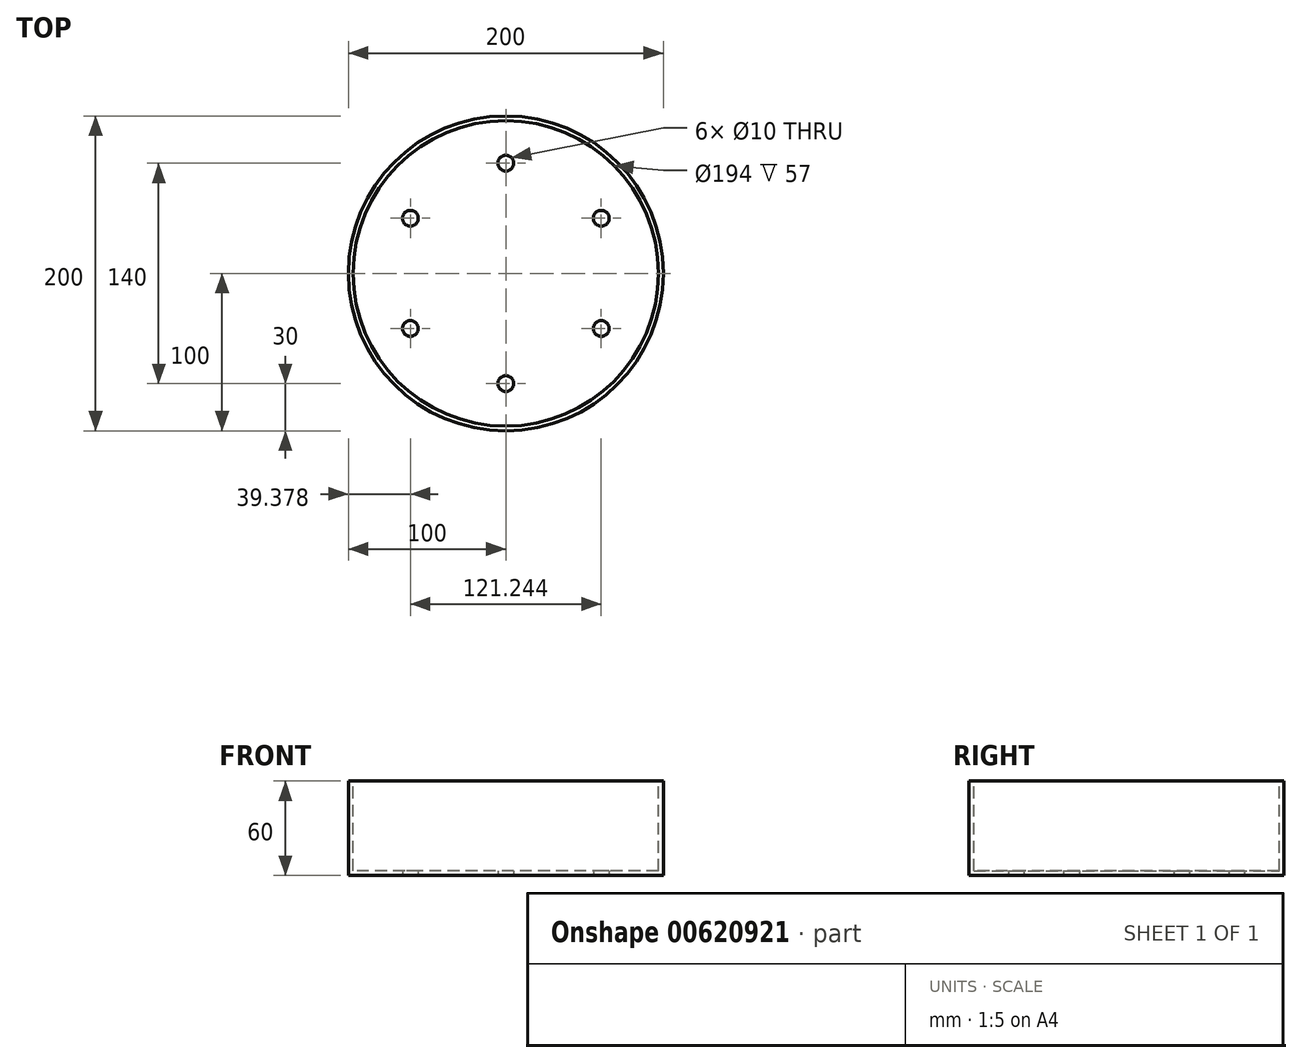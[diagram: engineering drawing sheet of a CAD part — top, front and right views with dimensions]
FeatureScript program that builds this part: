
annotation { "Feature Type Name" : "Feature", "Feature Type Description" : "" }
export const myFeature = defineFeature(function(context is Context, id is Id, definition is map)
    precondition{}
    {
        {
            var Q0;
            Q0=qCreatedBy(makeId("Top.planeOp"),FACE);
            var sketch = newSketch(context, id + "F0", { "sketchPlane" : qUnion([Q0])});
            skCircle(sketch, "E0", {"center": v(0, 0) * mm, "radius": 100 * mm});
            skLineSegment(sketch, "E1", {"start": v(0, 0) * mm, "end": v(0, 70) * mm});
            skLineSegment(sketch, "E2", {"start": v(0, 0) * mm, "end": v(60.62, 35) * mm});
            skLineSegment(sketch, "E3.MirrorCS", {"start": v(0, 0) * mm, "end": v(-60.62, 35) * mm});
            skLineSegment(sketch, "E4.MirrorCS", {"start": v(0, 0) * mm, "end": v(-60.62, -35) * mm});
            skLineSegment(sketch, "E5.MirrorCS", {"start": v(0, 0) * mm, "end": v(0, -70) * mm});
            skLineSegment(sketch, "E6.MirrorCS", {"start": v(0, 0) * mm, "end": v(60.62, -35) * mm});
            skCircle(sketch, "E7", {"center": v(0, 70) * mm, "radius": 5 * mm});
            skCircle(sketch, "E8", {"center": v(60.62, 35) * mm, "radius": 5 * mm});
            skCircle(sketch, "E9", {"center": v(60.62, -35) * mm, "radius": 5 * mm});
            skCircle(sketch, "E10", {"center": v(0, -70) * mm, "radius": 5 * mm});
            skCircle(sketch, "E11", {"center": v(-60.62, -35) * mm, "radius": 5 * mm});
            skCircle(sketch, "E12", {"center": v(-60.62, 35) * mm, "radius": 5 * mm});
            skSolve(sketch);
        }
        {
            var Q0;
            Q0=makeQuery(id+"F0.imprint","IMPRINT",FACE,{"disambiguationData":[TD([[makeQuery(id+"F0.imprint","IMPRINT",EDGE,{"derivedFrom":sQuery(id+"F0.wireOp",EDGE,"E0")}),1.0]])]});
            extrude(context, id + "F1", {"entities" : qUnion([Q0]), "depth" : 60 * mm, "offsetDistance" : 25 * mm});
        }
        {
            var Q0;
            Q0=makeQuery(id+"F1.opExtrude","CAP_FACE",FACE,{"disambiguationData":[OSD([sQuery(id+"F0.wireOp",EDGE,"E0"),sQuery(id+"F0.wireOp",EDGE,"E7"),sQuery(id+"F0.wireOp",EDGE,"E8"),sQuery(id+"F0.wireOp",EDGE,"E9"),sQuery(id+"F0.wireOp",EDGE,"E10"),sQuery(id+"F0.wireOp",EDGE,"E11"),sQuery(id+"F0.wireOp",EDGE,"E12")])],"isStart":false});
            var sketch = newSketch(context, id + "F2", { "sketchPlane" : qUnion([Q0])});
            skCircle(sketch, "E13", {"center": v(0, 0) * mm, "radius": 97 * mm});
            skSolve(sketch);
        }
        {
            var Q0;
            Q0 = qSketchRegion(id + "F2", true);
            var Q1;
            Q1=makeQuery(id+"F2.imprint","IMPRINT",FACE,{"disambiguationData":[TD([[makeQuery(id+"F2.imprint","IMPRINT",EDGE,{"derivedFrom":sQuery(id+"F2.wireOp",EDGE,"E13")}),1.0]])]});
            extrude(context, id + "F3", {"entities" : qUnion([Q0, Q1]), "operationType" : NewBodyOperationType.REMOVE, "oppositeDirection" : true, "depth" : 57 * mm, "offsetDistance" : 25 * mm});
        }
    });
